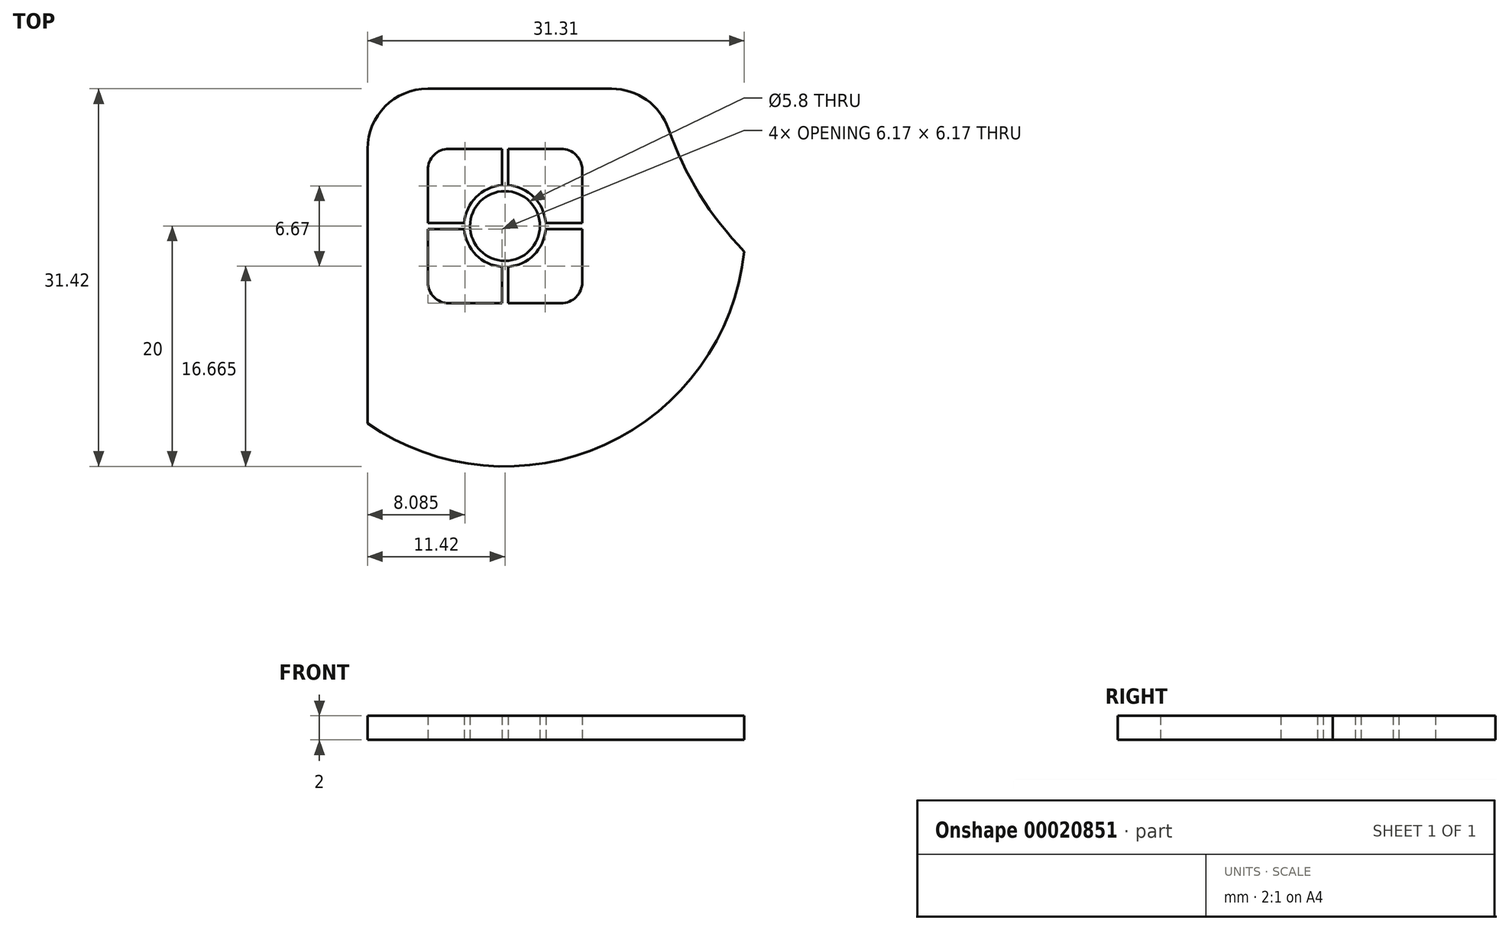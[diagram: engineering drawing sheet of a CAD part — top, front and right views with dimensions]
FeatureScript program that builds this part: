
annotation { "Feature Type Name" : "Feature", "Feature Type Description" : "" }
export const myFeature = defineFeature(function(context is Context, id is Id, definition is map)
    precondition{}
    {
        {
            var Q0;
            Q0=qCreatedBy(makeId("Top.planeOp"),FACE);
            var sketch = newSketch(context, id + "F0", { "sketchPlane" : qUnion([Q0])});
            skLineSegment(sketch, "E0.rect.bottom", {"start": v(56, -30) * mm, "end": v(-56, -30) * mm});
            skLineSegment(sketch, "E0.rect.top", {"start": v(56, 55) * mm, "end": v(-56, 55) * mm, "construction": true});
            skLineSegment(sketch, "E0.rect.left", {"start": v(56, -30) * mm, "end": v(56, 55) * mm});
            skLineSegment(sketch, "E0.rect.right", {"start": v(-56, -30) * mm, "end": v(-56, 55) * mm});
            skPoint(sketch, "E0.rect.middle", {"position": v(0, 12.5) * mm});
            skArc(sketch, "E1", {"start": v(56, 55) * mm, "mid": v(0, 80) * mm, "end": v(-56, 55) * mm});
            skCircle(sketch, "E2", {"center": v(0, 0) * mm, "radius": 6 * mm});
            skPoint(sketch, "E3.rect.middle", {"position": v(0, 20.57) * mm});
            skCircle(sketch, "E4", {"center": v(0, 49) * mm, "radius": 26 * mm});
            skLineSegment(sketch, "E5.rect.bottom", {"start": v(5.5, 12) * mm, "end": v(-5.5, 12) * mm});
            skLineSegment(sketch, "E5.rect.top", {"start": v(5.5, 18) * mm, "end": v(-5.5, 18) * mm});
            skLineSegment(sketch, "E5.rect.left", {"start": v(5.5, 12) * mm, "end": v(5.5, 18) * mm});
            skLineSegment(sketch, "E5.rect.right", {"start": v(-5.5, 12) * mm, "end": v(-5.5, 18) * mm});
            skPoint(sketch, "E5.rect.middle", {"position": v(0, 15) * mm});
            skCircle(sketch, "E6", {"center": v(0, -21) * mm, "radius": 3.5 * mm});
            skSolve(sketch);
        }
        {
            var Q0;
            Q0=qCreatedBy(makeId("Top.planeOp"),FACE);
            var sketch = newSketch(context, id + "F1", { "sketchPlane" : qUnion([Q0])});
            skLineSegment(sketch, "E7.rect.bottom", {"start": v(-36, 27.64) * mm, "end": v(-44, 27.64) * mm, "construction": true});
            skLineSegment(sketch, "E7.rect.top", {"start": v(-36, 35.64) * mm, "end": v(-44, 35.64) * mm, "construction": true});
            skLineSegment(sketch, "E7.rect.left", {"start": v(-36, 27.64) * mm, "end": v(-36, 35.64) * mm, "construction": true});
            skLineSegment(sketch, "E7.rect.right", {"start": v(-44, 27.64) * mm, "end": v(-44, 35.64) * mm, "construction": true});
            skPoint(sketch, "E7.rect.middle", {"position": v(-40, 31.64) * mm});
            skCircle(sketch, "E8", {"center": v(-44, 35.64) * mm, "radius": 2.42 * mm});
            skCircle(sketch, "E9", {"center": v(-36, 35.64) * mm, "radius": 2.42 * mm});
            skCircle(sketch, "E10", {"center": v(-36, 27.64) * mm, "radius": 2.42 * mm});
            skCircle(sketch, "E11", {"center": v(-44, 27.64) * mm, "radius": 2.42 * mm});
            skLineSegment(sketch, "E12", {"start": v(-53.94, 38.06) * mm, "end": v(-41.14, 38.06) * mm, "construction": true});
            skLineSegment(sketch, "E13", {"start": v(-41.5, 25.22) * mm, "end": v(-52.62, 25.22) * mm, "construction": true});
            skLineSegment(sketch, "E14", {"start": v(-54.48, 7.61) * mm, "end": v(49.55, 7.61) * mm, "construction": true});
            skLineSegment(sketch, "E15", {"start": v(0, 30.66) * mm, "end": v(0, -16.38) * mm, "construction": true});
            skPoint(sketch, "E16.MirrorP", {"position": v(-40, -16.42) * mm});
            skLineSegment(sketch, "E17.MirrorCS", {"start": v(-53.94, -22.84) * mm, "end": v(-41.14, -22.84) * mm, "construction": true});
            skLineSegment(sketch, "E18.MirrorCS", {"start": v(-36, -12.42) * mm, "end": v(-44, -12.42) * mm, "construction": true});
            skLineSegment(sketch, "E19.MirrorCS", {"start": v(-36, -20.42) * mm, "end": v(-44, -20.42) * mm, "construction": true});
            skCircle(sketch, "E20.MirrorC", {"center": v(-44, -12.42) * mm, "radius": 2.42 * mm});
            skLineSegment(sketch, "E21.MirrorCS", {"start": v(-36, -12.42) * mm, "end": v(-36, -20.42) * mm, "construction": true});
            skLineSegment(sketch, "E22.MirrorCS", {"start": v(-41.5, -10) * mm, "end": v(-52.62, -10) * mm, "construction": true});
            skLineSegment(sketch, "E23.MirrorCS", {"start": v(-44, -12.42) * mm, "end": v(-44, -20.42) * mm, "construction": true});
            skCircle(sketch, "E24.MirrorC", {"center": v(-44, -20.42) * mm, "radius": 2.42 * mm});
            skCircle(sketch, "E25.MirrorC", {"center": v(-36, -20.42) * mm, "radius": 2.42 * mm});
            skCircle(sketch, "E26.MirrorC", {"center": v(-36, -12.42) * mm, "radius": 2.42 * mm});
            skLineSegment(sketch, "E27.MirrorCS", {"start": v(53.94, -22.84) * mm, "end": v(41.14, -22.84) * mm, "construction": true});
            skLineSegment(sketch, "E28.MirrorCS", {"start": v(41.5, -10) * mm, "end": v(52.62, -10) * mm, "construction": true});
            skCircle(sketch, "E29.MirrorC", {"center": v(44, -20.42) * mm, "radius": 2.42 * mm});
            skLineSegment(sketch, "E30.MirrorCS", {"start": v(41.5, 25.22) * mm, "end": v(52.62, 25.22) * mm, "construction": true});
            skLineSegment(sketch, "E31.MirrorCS", {"start": v(53.94, 38.06) * mm, "end": v(41.14, 38.06) * mm, "construction": true});
            skPoint(sketch, "E32.MirrorP", {"position": v(40, 31.64) * mm});
            skCircle(sketch, "E33.MirrorC", {"center": v(36, -12.42) * mm, "radius": 2.42 * mm});
            skCircle(sketch, "E34.MirrorC", {"center": v(44, 27.64) * mm, "radius": 2.42 * mm});
            skCircle(sketch, "E35.MirrorC", {"center": v(36, 27.64) * mm, "radius": 2.42 * mm});
            skCircle(sketch, "E36.MirrorC", {"center": v(36, 35.64) * mm, "radius": 2.42 * mm});
            skCircle(sketch, "E37.MirrorC", {"center": v(44, 35.64) * mm, "radius": 2.42 * mm});
            skLineSegment(sketch, "E38.MirrorCS", {"start": v(44, 27.64) * mm, "end": v(44, 35.64) * mm, "construction": true});
            skLineSegment(sketch, "E39.MirrorCS", {"start": v(36, 27.64) * mm, "end": v(36, 35.64) * mm, "construction": true});
            skLineSegment(sketch, "E40.MirrorCS", {"start": v(36, 27.64) * mm, "end": v(44, 27.64) * mm, "construction": true});
            skLineSegment(sketch, "E41.MirrorCS", {"start": v(36, 35.64) * mm, "end": v(44, 35.64) * mm, "construction": true});
            skLineSegment(sketch, "E42.MirrorCS", {"start": v(36, -20.42) * mm, "end": v(44, -20.42) * mm, "construction": true});
            skCircle(sketch, "E43.MirrorC", {"center": v(44, -12.42) * mm, "radius": 2.42 * mm});
            skLineSegment(sketch, "E44.MirrorCS", {"start": v(36, -12.42) * mm, "end": v(44, -12.42) * mm, "construction": true});
            skPoint(sketch, "E45.MirrorP", {"position": v(40, -16.42) * mm});
            skLineSegment(sketch, "E46.MirrorCS", {"start": v(36, -12.42) * mm, "end": v(36, -20.42) * mm, "construction": true});
            skLineSegment(sketch, "E47.MirrorCS", {"start": v(44, -12.42) * mm, "end": v(44, -20.42) * mm, "construction": true});
            skCircle(sketch, "E48.MirrorC", {"center": v(36, -20.42) * mm, "radius": 2.42 * mm});
            skLineSegment(sketch, "E49", {"start": v(-46.42, 39.36) * mm, "end": v(-46.42, 21.25) * mm, "construction": true});
            skLineSegment(sketch, "E50", {"start": v(46.42, 42.62) * mm, "end": v(46.42, 20.5) * mm, "construction": true});
            skSolve(sketch);
        }
        {
            var Q0;
            Q0=qCreatedBy(makeId("Top.planeOp"),FACE);
            var sketch = newSketch(context, id + "F2", { "sketchPlane" : qUnion([Q0])});
            skLineSegment(sketch, "E51", {"start": v(-51.42, 38.06) * mm, "end": v(-51.42, -22.84) * mm});
            skLineSegment(sketch, "E52", {"start": v(-46.42, -27.84) * mm, "end": v(0, -27.84) * mm});
            skLineSegment(sketch, "E53", {"start": v(0, -27.84) * mm, "end": v(0, 21) * mm});
            skLineSegment(sketch, "E54", {"start": v(-31.13, 43.06) * mm, "end": v(-46.42, 43.06) * mm});
            skArc(sketch, "E55", {"start": v(-26.42, 39.72) * mm, "mid": v(-16.19, 26.15) * mm, "end": v(0, 21) * mm});
            skPoint(sketch, "E56.visualSharp", {"position": v(-51.42, 43.06) * mm});
            skArc(sketch, "E56.filletArc", {"start": v(-46.42, 43.06) * mm, "mid": v(-49.96, 41.6) * mm, "end": v(-51.42, 38.06) * mm});
            skPoint(sketch, "E57.visualSharp", {"position": v(-27.36, 43.06) * mm});
            skArc(sketch, "E57.filletArc", {"start": v(-26.42, 39.72) * mm, "mid": v(-28.24, 42.14) * mm, "end": v(-31.13, 43.06) * mm});
            skPoint(sketch, "E58.visualSharp", {"position": v(-51.42, -27.84) * mm});
            skArc(sketch, "E58.filletArc", {"start": v(-51.42, -22.84) * mm, "mid": v(-49.96, -26.38) * mm, "end": v(-46.42, -27.84) * mm});
            skCircle(sketch, "E59", {"center": v(-40, 31.64) * mm, "radius": 3.4 * mm});
            skCircle(sketch, "E60", {"center": v(-40, 31.64) * mm, "radius": 2.9 * mm});
            skLineSegment(sketch, "E61.rect.bottom", {"start": v(-44.67, 38.06) * mm, "end": v(-35.33, 38.06) * mm});
            skLineSegment(sketch, "E61.rect.top", {"start": v(-44.67, 25.22) * mm, "end": v(-35.33, 25.22) * mm});
            skLineSegment(sketch, "E61.rect.left", {"start": v(-46.42, 36.31) * mm, "end": v(-46.42, 26.97) * mm});
            skLineSegment(sketch, "E61.rect.right", {"start": v(-33.58, 36.31) * mm, "end": v(-33.58, 26.97) * mm});
            skLineSegment(sketch, "E62.rect.bottom", {"start": v(-46.42, 31.89) * mm, "end": v(-33.58, 31.89) * mm});
            skLineSegment(sketch, "E62.rect.top", {"start": v(-46.42, 31.39) * mm, "end": v(-33.58, 31.39) * mm});
            skLineSegment(sketch, "E62.rect.left", {"start": v(-46.42, 31.89) * mm, "end": v(-46.42, 31.39) * mm});
            skLineSegment(sketch, "E62.rect.right", {"start": v(-33.58, 31.89) * mm, "end": v(-33.58, 31.39) * mm});
            skLineSegment(sketch, "E63.rect.bottom", {"start": v(-39.75, 38.06) * mm, "end": v(-40.25, 38.06) * mm});
            skLineSegment(sketch, "E63.rect.top", {"start": v(-39.75, 25.22) * mm, "end": v(-40.25, 25.22) * mm});
            skLineSegment(sketch, "E63.rect.left", {"start": v(-39.75, 38.06) * mm, "end": v(-39.75, 25.22) * mm});
            skLineSegment(sketch, "E63.rect.right", {"start": v(-40.25, 38.06) * mm, "end": v(-40.25, 25.22) * mm});
            skPoint(sketch, "E64.visualSharp", {"position": v(-33.58, 38.06) * mm});
            skArc(sketch, "E64.filletArc", {"start": v(-33.58, 36.31) * mm, "mid": v(-34.1, 37.55) * mm, "end": v(-35.33, 38.06) * mm});
            skPoint(sketch, "E65.visualSharp", {"position": v(-33.58, 25.22) * mm});
            skArc(sketch, "E65.filletArc", {"start": v(-35.33, 25.22) * mm, "mid": v(-34.1, 25.73) * mm, "end": v(-33.58, 26.97) * mm});
            skPoint(sketch, "E66.visualSharp", {"position": v(-46.42, 25.22) * mm});
            skArc(sketch, "E66.filletArc", {"start": v(-46.42, 26.97) * mm, "mid": v(-45.9, 25.73) * mm, "end": v(-44.67, 25.22) * mm});
            skArc(sketch, "E67.filletArc", {"start": v(-44.67, 38.06) * mm, "mid": v(-45.9, 37.55) * mm, "end": v(-46.42, 36.31) * mm});
            skSolve(sketch);
        }
        {
            var Q0;
            Q0=qCreatedBy(makeId("Top.planeOp"),FACE);
            var sketch = newSketch(context, id + "F3", { "sketchPlane" : qUnion([Q0])});
            skLineSegment(sketch, "E68.0", {"start": v(-46.42, 36.31) * mm, "end": v(-46.42, 26.97) * mm});
            skArc(sketch, "E68.1", {"start": v(-44.67, 38.06) * mm, "mid": v(-45.9, 37.55) * mm, "end": v(-46.42, 36.31) * mm});
            skLineSegment(sketch, "E68.2", {"start": v(-44.67, 38.06) * mm, "end": v(-35.33, 38.06) * mm});
            skArc(sketch, "E68.3", {"start": v(-33.58, 36.31) * mm, "mid": v(-34.1, 37.55) * mm, "end": v(-35.33, 38.06) * mm});
            skLineSegment(sketch, "E68.4", {"start": v(-33.58, 36.31) * mm, "end": v(-33.58, 26.97) * mm});
            skArc(sketch, "E68.5", {"start": v(-35.33, 25.22) * mm, "mid": v(-34.1, 25.73) * mm, "end": v(-33.58, 26.97) * mm});
            skLineSegment(sketch, "E68.6", {"start": v(-44.67, 25.22) * mm, "end": v(-35.33, 25.22) * mm});
            skArc(sketch, "E68.7", {"start": v(-46.42, 26.97) * mm, "mid": v(-45.9, 25.73) * mm, "end": v(-44.67, 25.22) * mm});
            skArc(sketch, "E68.8", {"start": v(-40.25, 35.03) * mm, "mid": v(-42.4, 34.04) * mm, "end": v(-43.4, 31.89) * mm});
            skCircle(sketch, "E68.9", {"center": v(-40, 31.64) * mm, "radius": 2.9 * mm});
            skLineSegment(sketch, "E68.10", {"start": v(-46.42, 31.39) * mm, "end": v(-43.4, 31.39) * mm});
            skLineSegment(sketch, "E68.11", {"start": v(-46.42, 31.89) * mm, "end": v(-43.4, 31.89) * mm});
            skLineSegment(sketch, "E68.12", {"start": v(-40.25, 38.06) * mm, "end": v(-40.25, 35.03) * mm});
            skLineSegment(sketch, "E68.13", {"start": v(-39.75, 38.06) * mm, "end": v(-39.75, 35.03) * mm});
            skLineSegment(sketch, "E68.14", {"start": v(-51.42, 38.06) * mm, "end": v(-51.42, 15.22) * mm});
            skArc(sketch, "E68.15", {"start": v(-46.42, 43.06) * mm, "mid": v(-49.96, 41.6) * mm, "end": v(-51.42, 38.06) * mm});
            skLineSegment(sketch, "E68.16", {"start": v(-31.13, 43.06) * mm, "end": v(-46.42, 43.06) * mm});
            skArc(sketch, "E68.17", {"start": v(-26.42, 39.72) * mm, "mid": v(-28.24, 42.14) * mm, "end": v(-31.13, 43.06) * mm});
            skArc(sketch, "E68.18", {"start": v(-26.42, 39.72) * mm, "mid": v(-23.82, 34.28) * mm, "end": v(-20.11, 29.52) * mm});
            skLineSegment(sketch, "E69.trimOffspring", {"start": v(-40.25, 28.25) * mm, "end": v(-40.25, 25.22) * mm});
            skLineSegment(sketch, "E70.trimOffspring", {"start": v(-36.6, 31.89) * mm, "end": v(-33.58, 31.89) * mm});
            skLineSegment(sketch, "E71.trimOffspring", {"start": v(-39.75, 28.25) * mm, "end": v(-39.75, 25.22) * mm});
            skLineSegment(sketch, "E72.trimOffspring", {"start": v(-36.6, 31.39) * mm, "end": v(-33.58, 31.39) * mm});
            skArc(sketch, "E73.trimOffspring", {"start": v(-43.4, 31.39) * mm, "mid": v(-42.4, 29.24) * mm, "end": v(-40.25, 28.25) * mm});
            skArc(sketch, "E74.trimOffspring", {"start": v(-39.75, 28.25) * mm, "mid": v(-37.6, 29.24) * mm, "end": v(-36.6, 31.39) * mm});
            skArc(sketch, "E75.trimOffspring", {"start": v(-36.6, 31.89) * mm, "mid": v(-37.6, 34.04) * mm, "end": v(-39.75, 35.03) * mm});
            skArc(sketch, "E76", {"start": v(-51.42, 15.22) * mm, "mid": v(-31.7, 13.45) * mm, "end": v(-20.11, 29.52) * mm});
            skPoint(sketch, "E77.orphan", {"position": v(-51.42, -22.84) * mm});
            skPoint(sketch, "E78.orphan", {"position": v(0, 21) * mm});
            skSolve(sketch);
        }
        {
            var Q0;
            {var subQ12=sQuery(id+"F3.wireOp",EDGE,"E68.1");Q0=makeQuery(id+"F3.imprint","IMPRINT",FACE,{"disambiguationData":[TD([[makeQuery(id+"F3.imprint","IMPRINT",EDGE,{"derivedFrom":subQ12}),-1.0]])]});}
            var Q1;
            Q1=makeQuery(id+"F3.imprint","IMPRINT",FACE,{"disambiguationData":[TD([[makeQuery(id+"F3.imprint","IMPRINT",EDGE,{"derivedFrom":sQuery(id+"F3.wireOp",EDGE,"E68.8")}),1.0]])]});
            extrude(context, id + "F4", {"entities" : qUnion([Q0, Q1]), "depth" : 2 * mm});
        }
    });
